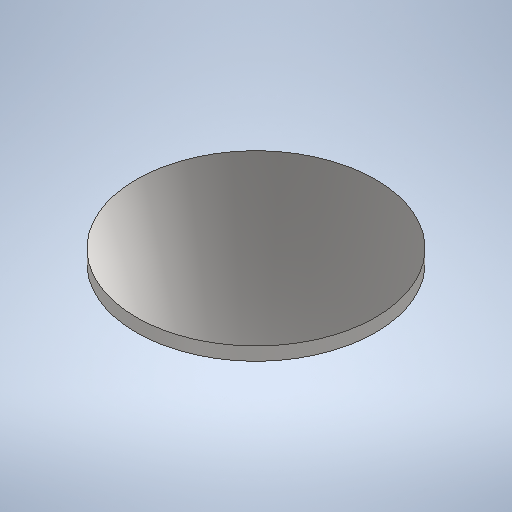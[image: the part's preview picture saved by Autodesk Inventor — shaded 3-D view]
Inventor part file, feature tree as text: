
AUTODESK INVENTOR PART (.ipt)
format: ipt  version: 2025.1 (Build 291241020, 241B)  size: 240,128 bytes
history: native  units: mm
features: extrude x1, sketch x1
ambient origin geometry x8: Origin, YZ Plane, XZ Plane, XY Plane, X Axis, Y Axis, Z Axis, Center Point
bodies: Solid1 (feature_tree)
feature tree (2):
  extrude  "Extrusion1"  Depth=1.1mm TaperAngle=0.0deg
  sketch  "Sketch1"  dims[d0=20.0mm d1=1.1mm d2=0.0mm]
